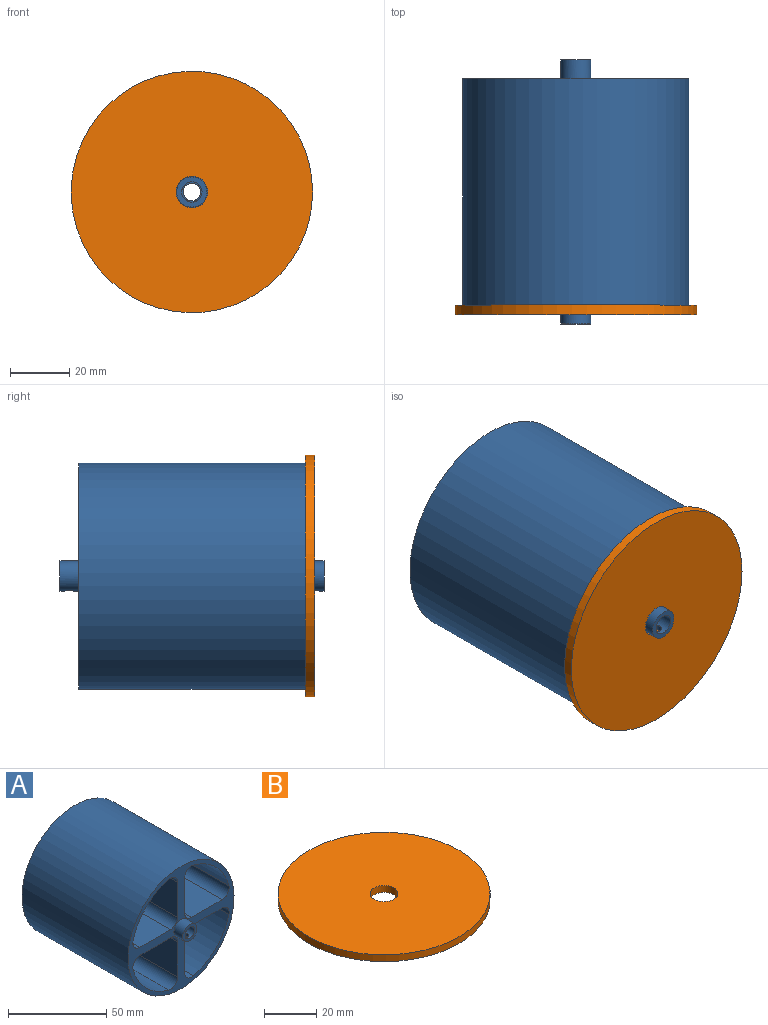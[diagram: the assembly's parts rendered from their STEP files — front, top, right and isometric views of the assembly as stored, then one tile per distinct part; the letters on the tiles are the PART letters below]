
ASSEMBLY  parts=2 mates=1
PART A: 38 faces, bbox 76.2x88.9x76.2 mm
  f0: plane 6.86x6.86mm, normal (0,-1,0), area 10.1mm2, adj f2,f33
  f1: plane 6.86x6.86mm, normal (0,1,0), area 10.1mm2, adj f2,f3
  f2: cylinder r=2.92mm len=76.2mm, axis (0,1,0), area 1398.5mm2, adj f0,f1
  f3: cylinder r=3.43mm len=6.86mm, axis (0,-1,0), area 128.7mm2, adj f1,f4,f37
  f4: plane 10.16x10.16mm, normal (0,1,0), area 44.1mm2, adj f3,f5
  f5: cylinder r=5.08mm len=10.16mm, axis (0,-1,0), area 194.7mm2, adj f4,f32,f37
  f6: cylinder r=5.08mm len=76.2mm, axis (0,1,0), area 705.9mm2, adj f7,f11,f30,f32
  f7: plane 76.2x21.89mm, normal (-1,0,0), area 1668.2mm2, adj f6,f8,f30,f32
  f8: cylinder r=5.08mm len=76.2mm, axis (0,-1,0), area 608mm2, adj f7,f9,f30,f32
  f9: plane 76.2x21.89mm, normal (0,0,1), area 1668.2mm2, adj f8,f10,f30,f32
  f10: cylinder r=5.08mm len=76.2mm, axis (0,1,0), area 705.9mm2, adj f9,f11,f30,f32
  f11: cylinder r=35.56mm len=76.2mm, axis (0,1,0), area 2887mm2, adj f6,f10,f30,f32
  f12: cylinder r=5.08mm len=76.2mm, axis (0,1,0), area 705.9mm2, adj f13,f17,f30,f32
  f13: plane 76.2x21.89mm, normal (1,0,0), area 1668.2mm2, adj f12,f14,f30,f32
  f14: cylinder r=5.08mm len=76.2mm, axis (0,-1,0), area 608mm2, adj f13,f15,f30,f32
  f15: plane 76.2x21.89mm, normal (0,0,-1), area 1668.2mm2, adj f14,f16,f30,f32
  f16: cylinder r=5.08mm len=76.2mm, axis (0,1,0), area 705.9mm2, adj f15,f17,f30,f32
  f17: cylinder r=35.56mm len=76.2mm, axis (0,1,0), area 2887mm2, adj f12,f16,f30,f32
  f18: cylinder r=38.1mm len=76.2mm, axis (0,1,0), area 18241.5mm2, adj f30,f32
  f19: cylinder r=5.08mm len=76.2mm, axis (0,1,0), area 705.9mm2, adj f20,f24,f30,f32
  f20: cylinder r=35.56mm len=76.2mm, axis (0,1,0), area 2887mm2, adj f19,f21,f30,f32
  f21: cylinder r=5.08mm len=76.2mm, axis (0,1,0), area 705.9mm2, adj f20,f22,f30,f32
  f22: plane 76.2x21.89mm, normal (0,0,-1), area 1668.2mm2, adj f21,f23,f30,f32
  f23: cylinder r=5.08mm len=76.2mm, axis (0,-1,0), area 608mm2, adj f22,f24,f30,f32
  f24: plane 76.2x21.89mm, normal (-1,0,0), area 1668.2mm2, adj f19,f23,f30,f32
  f25: cylinder r=5.08mm len=76.2mm, axis (0,1,0), area 705.9mm2, adj f26,f30,f31,f32
  f26: plane 76.2x21.89mm, normal (0,0,1), area 1668.2mm2, adj f25,f27,f30,f32
  f27: cylinder r=5.08mm len=76.2mm, axis (0,-1,0), area 608mm2, adj f26,f28,f30,f32
  f28: plane 76.2x21.89mm, normal (1,0,0), area 1668.2mm2, adj f27,f29,f30,f32
  f29: cylinder r=5.08mm len=76.2mm, axis (0,1,0), area 705.9mm2, adj f28,f30,f31,f32
  f30: plane 76.2x76.2mm, normal (0,-1,0), area 1293.1mm2, adj f6,f7,f8,f9,f10,f11,f12,f13
  f31: cylinder r=35.56mm len=76.2mm, axis (0,1,0), area 2887mm2, adj f25,f29,f30,f32
  f32: plane 76.2x76.2mm, normal (0,1,0), area 1293.1mm2, adj f5,f6,f7,f8,f9,f10,f11,f12
  f33: cylinder r=3.43mm len=6.86mm, axis (0,-1,0), area 128.7mm2, adj f0,f35,f36
  f34: cylinder r=5.08mm len=10.16mm, axis (0,-1,0), area 194.7mm2, adj f30,f35,f36
  f35: plane 10.16x10.16mm, normal (0,-1,0), area 44.1mm2, adj f33,f34
  f36: cylinder r=1.59mm len=3.18mm, axis (0,0,1), area 17.1mm2, adj f33,f34
  f37: cylinder r=1.59mm len=3.18mm, axis (0,0,1), area 17.1mm2, adj f3,f5
PART B: 4 faces, bbox 81.3x81.3x3.2 mm
  f0: cylinder r=5.33mm len=10.67mm, axis (0,0,-1), area 106.4mm2, adj f2,f3
  f1: cylinder r=40.64mm len=81.28mm, axis (0,0,-1), area 810.7mm2, adj f2,f3
  f2: plane 81.28x81.28mm, normal (0,0,1), area 5099.3mm2, adj f0,f1
  f3: plane 81.28x81.28mm, normal (0,0,-1), area 5099.3mm2, adj f0,f1
PLACE A t=(-54.87,16.69,18.26)mm
PLACE B rot(axis=(-1,0,0),90deg) t=(-54.87,-62.69,18.26)mm
MATE fastened B.f0 <-> A.f11  axis (0,1,0) through (-54.87,-59.51,18.26)mm
